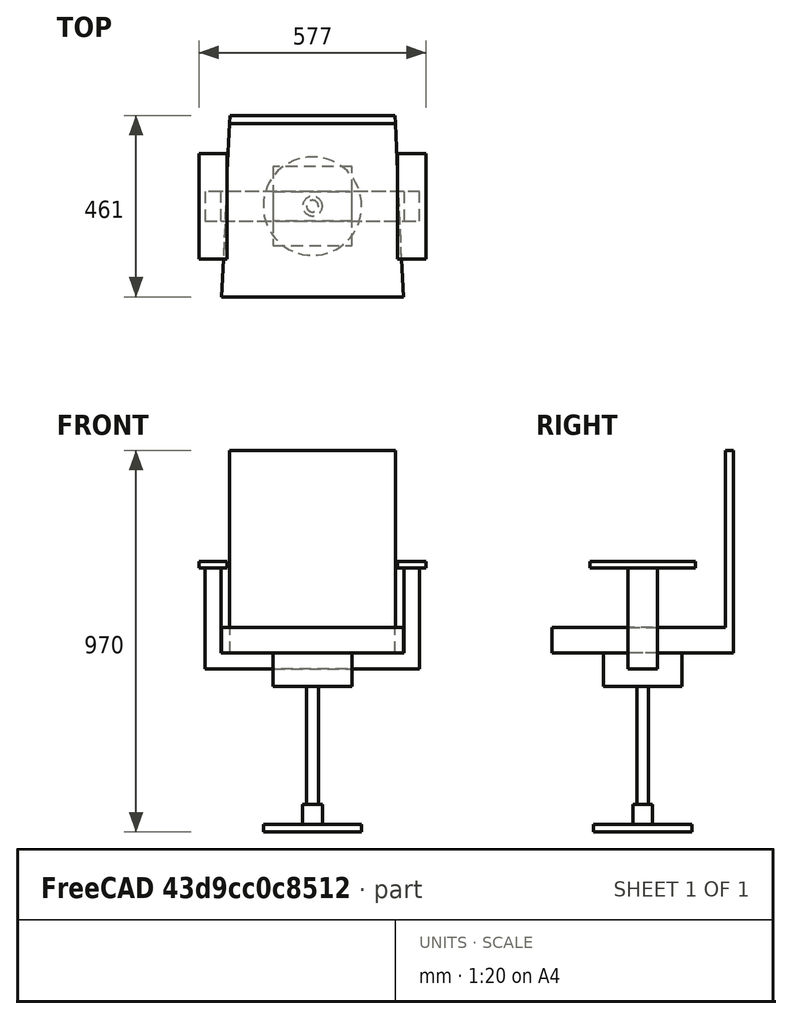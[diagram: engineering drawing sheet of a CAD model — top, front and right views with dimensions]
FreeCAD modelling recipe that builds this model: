
FCSTD DOCUMENT  (FreeCAD 1.0R39109 (Git))
Label: chair02_00503
License: All rights reserved
LicenseURL: https://en.wikipedia.org/wiki/All_rights_reserved
objects: Sketcher::SketchObject×10, PartDesign::Pad×10, TechDraw::DrawViewDimension×9, TechDraw::DrawViewAnnotation×9, PartDesign::Body×5, PartDesign::ShapeBinder×4, TechDraw::DrawSVGTemplate×3, TechDraw::DrawProjGroupItem×3, TechDraw::DrawPage×3, TechDraw::DrawViewSection×3, App::Part×1
note: 77 computed .brp shape members not serialized (recipe doc carries the construction recipe); baked Part::Feature solids carry a one-line shape summary decoded from their .brp

FEATURE [Sketcher::SketchObject] Sketch
  ArcFitTolerance = 1e-06
  AttachmentSupport = -> [XY_Plane]
  FullyConstrained = true
  MakeInternals = false
  MapMode = 5
  sketch-geometry (1):
    g0: Circle CenterX=0 CenterY=0 CenterZ=0 NormalX=0 NormalY=0 NormalZ=1 AngleXU=0 Radius=125
  constraints (2):
    c: Diameter(g0) = 250
    c: Coincident(g0,g-1)
FEATURE [PartDesign::Pad] Pad
  Direction = (0,0,1)
  Length = 20
  Length2 = 10
  Profile = -> Sketch
  ReferenceAxis = -> Sketch [N_Axis]
  Refine = true
  Suppressed = false
  Type = 0
FEATURE [Sketcher::SketchObject] Sketch001
  ArcFitTolerance = 1e-06
  AttachmentSupport = -> [Pad]
  FullyConstrained = true
  MakeInternals = false
  MapMode = 5
  Placement = pos=(0,0,20) rot=(0,0,1;0rad)
  sketch-geometry (1):
    g0: Circle CenterX=0 CenterY=0 CenterZ=0 NormalX=0 NormalY=0 NormalZ=1 AngleXU=0 Radius=25
  constraints (2):
    c: Diameter(g0) = 50
    c: Coincident(g0,g-1)
FEATURE [PartDesign::Pad] Pad001
  BaseFeature = -> Pad
  Direction = (0,0,1)
  Length = 50
  Length2 = 10
  Profile = -> Sketch001
  ReferenceAxis = -> Sketch001 [N_Axis]
  Refine = true
  Suppressed = false
  Type = 0
FEATURE [PartDesign::Body] Body  label="Body1"
  AllowCompound = false
  Group = -> [Sketch,Pad,Sketch001,Pad001]
  Origin = -> Origin
  Tip = -> Pad001
FEATURE [PartDesign::ShapeBinder] CopyPad001  label="Body2_Sketch_P.lane"
  Placement = pos=(0,0,50) rot=(0,0,1;0rad)
  TraceSupport = false
FEATURE [Sketcher::SketchObject] Sketch002
  ArcFitTolerance = 1e-06
  AttachmentSupport = -> [CopyPad001]
  FullyConstrained = true
  MakeInternals = false
  MapMode = 5
  Placement = pos=(0,0,70) rot=(0,0,1;0rad)
  sketch-geometry (1):
    g0: Circle CenterX=0 CenterY=0 CenterZ=0 NormalX=0 NormalY=0 NormalZ=1 AngleXU=0 Radius=15
  constraints (2):
    c: Diameter(g0) = 30
    c: Coincident(g0,g-1)
FEATURE [PartDesign::Pad] Pad002
  Direction = (0,0,1)
  Length = 300
  Length2 = 10
  Placement = pos=(0,0,50) rot=(0,0,1;0rad)
  Profile = -> Sketch002
  ReferenceAxis = -> Sketch002 [N_Axis]
  Refine = true
  Suppressed = false
  Type = 0
FEATURE [PartDesign::Body] Body001  label="Body2"
  AllowCompound = false
  Group = -> [CopyPad001,Sketch002,Pad002]
  Origin = -> Origin001
  Tip = -> Pad002
FEATURE [PartDesign::ShapeBinder] CopyPad002  label="Body3_Sketch_Plane"
  Placement = pos=(0,0,300) rot=(0,0,1;0rad)
  TraceSupport = false
FEATURE [Sketcher::SketchObject] Sketch003
  ArcFitTolerance = 1e-06
  AttachmentSupport = -> [CopyPad002]
  FullyConstrained = true
  MakeInternals = false
  MapMode = 5
  Placement = pos=(0,0,370) rot=(0,0,1;0rad)
  sketch-geometry (5):
    g0: LineSegment StartX=-100 StartY=-100 StartZ=0 EndX=100 EndY=-100 EndZ=0
    g1: LineSegment StartX=100 StartY=-100 StartZ=0 EndX=100 EndY=100 EndZ=0
    g2: LineSegment StartX=100 StartY=100 StartZ=0 EndX=-100 EndY=100 EndZ=0
    g3: LineSegment StartX=-100 StartY=100 StartZ=0 EndX=-100 EndY=-100 EndZ=0
    g4: GeomPoint [constr] X=0 Y=0 Z=0
  constraints (12):
    c: Coincident(g0,g1)
    c: Coincident(g1,g2)
    c: Coincident(g2,g3)
    c: Coincident(g3,g0)
    c: Horizontal(g0)
    c: Horizontal(g2)
    c: Vertical(g1)
    c: Vertical(g3)
    c: Symmetric(g2,g0,g4)
    c: Distance(g1,g3) = 200
    c: Distance(g0,g2) = 200
    c: Coincident(g4,g-1)
FEATURE [PartDesign::Pad] Pad003
  Direction = (0,0,1)
  Length = 45
  Length2 = 10
  Placement = pos=(0,0,300) rot=(0,0,1;0rad)
  Profile = -> Sketch003
  ReferenceAxis = -> Sketch003 [N_Axis]
  Refine = true
  Suppressed = false
  Type = 0
FEATURE [PartDesign::ShapeBinder] CopyPad003  label="Body4_Sketch_Plane"
  Placement = pos=(0,0,45) rot=(0,0,1;0rad)
  TraceSupport = false
FEATURE [Sketcher::SketchObject] Sketch004
  ArcFitTolerance = 1e-06
  AttachmentSupport = -> [CopyPad003]
  FullyConstrained = true
  MakeInternals = false
  MapMode = 5
  Placement = pos=(0,0,415) rot=(0,0,1;0rad)
  sketch-geometry (5):
    g0: LineSegment StartX=-272.5 StartY=-37.5 StartZ=0 EndX=272.5 EndY=-37.5 EndZ=0
    g1: LineSegment StartX=272.5 StartY=-37.5 StartZ=0 EndX=272.5 EndY=37.5 EndZ=0
    g2: LineSegment StartX=272.5 StartY=37.5 StartZ=0 EndX=-272.5 EndY=37.5 EndZ=0
    g3: LineSegment StartX=-272.5 StartY=37.5 StartZ=0 EndX=-272.5 EndY=-37.5 EndZ=0
    g4: GeomPoint [constr] X=0 Y=0 Z=0
  constraints (12):
    c: Coincident(g0,g1)
    c: Coincident(g1,g2)
    c: Coincident(g2,g3)
    c: Coincident(g3,g0)
    c: Horizontal(g0)
    c: Horizontal(g2)
    c: Vertical(g1)
    c: Vertical(g3)
    c: Symmetric(g2,g0,g4)
    c: Distance(g1,g3) = 545
    c: Distance(g0,g2) = 75
    c: Coincident(g4,g-1)
FEATURE [PartDesign::Pad] Pad004
  Direction = (0,0,1)
  Length = 40
  Length2 = 10
  Placement = pos=(0,0,45) rot=(0,0,1;0rad)
  Profile = -> Sketch004
  ReferenceAxis = -> Sketch004 [N_Axis]
  Refine = true
  Suppressed = false
  Type = 0
FEATURE [Sketcher::SketchObject] Sketch005
  ArcFitTolerance = 1e-06
  AttachmentSupport = -> [Pad004]
  ExternalGeometry = -> [Pad004]
  FullyConstrained = true
  MakeInternals = false
  MapMode = 5
  Placement = pos=(0,0,455) rot=(0,0,1;0rad)
  sketch-geometry (8):
    g0: LineSegment StartX=-272.5 StartY=37.5 StartZ=0 EndX=-272.5 EndY=-37.5 EndZ=0
    g1: LineSegment StartX=-272.5 StartY=-37.5 StartZ=0 EndX=-232.5 EndY=-37.5 EndZ=0
    g2: LineSegment StartX=-232.5 StartY=-37.5 StartZ=0 EndX=-232.5 EndY=37.5 EndZ=0
    g3: LineSegment StartX=-232.5 StartY=37.5 StartZ=0 EndX=-272.5 EndY=37.5 EndZ=0
    g4: LineSegment StartX=272.5 StartY=37.5 StartZ=0 EndX=232.5 EndY=37.5 EndZ=0
    g5: LineSegment StartX=232.5 StartY=37.5 StartZ=0 EndX=232.5 EndY=-37.5 EndZ=0
    g6: LineSegment StartX=232.5 StartY=-37.5 StartZ=0 EndX=272.5 EndY=-37.5 EndZ=0
    g7: LineSegment StartX=272.5 StartY=-37.5 StartZ=0 EndX=272.5 EndY=37.5 EndZ=0
  constraints (22):
    c: Coincident(g0,g1)
    c: Coincident(g1,g2)
    c: Coincident(g2,g3)
    c: Coincident(g3,g0)
    c: Vertical(g0)
    c: Vertical(g2)
    c: Horizontal(g1)
    c: Horizontal(g3)
    c: Coincident(g0,g-3)
    c: PointOnObject(g1,g-4)
    c: DistanceX(g3,g3) = 40
    c: Coincident(g4,g5)
    c: Coincident(g5,g6)
    c: Coincident(g6,g7)
    c: Coincident(g7,g4)
    c: Horizontal(g4)
    c: Horizontal(g6)
    c: Vertical(g5)
    c: Vertical(g7)
    c: Coincident(g4,g-3)
    c: PointOnObject(g5,g-4)
    c: Equal(g4,g3)
FEATURE [PartDesign::Pad] Pad005
  BaseFeature = -> Pad004
  Direction = (0,0,1)
  Length = 216
  Length2 = 10
  Placement = pos=(0,0,45) rot=(0,0,1;0rad)
  Profile = -> Sketch005
  ReferenceAxis = -> Sketch005 [N_Axis]
  Refine = true
  Suppressed = false
  Type = 0
FEATURE [Sketcher::SketchObject] Sketch006
  ArcFitTolerance = 1e-06
  AttachmentSupport = -> [Pad005]
  ExternalGeometry = -> [Pad005]
  FullyConstrained = true
  MakeInternals = false
  MapMode = 5
  Placement = pos=(0,0,671) rot=(0,0,1;0rad)
  sketch-geometry (16):
    g0: LineSegment StartX=-288.5 StartY=134 StartZ=0 EndX=-288.5 EndY=-134 EndZ=0
    g1: LineSegment StartX=-288.5 StartY=-134 StartZ=0 EndX=-216.5 EndY=-134 EndZ=0
    g2: LineSegment StartX=-216.5 StartY=-134 StartZ=0 EndX=-216.5 EndY=134 EndZ=0
    g3: LineSegment StartX=-216.5 StartY=134 StartZ=0 EndX=-288.5 EndY=134 EndZ=0
    g4: LineSegment StartX=216.5 StartY=134 StartZ=0 EndX=216.5 EndY=-134 EndZ=0
    g5: LineSegment StartX=216.5 StartY=-134 StartZ=0 EndX=288.5 EndY=-134 EndZ=0
    g6: LineSegment StartX=288.5 StartY=-134 StartZ=0 EndX=288.5 EndY=134 EndZ=0
    g7: LineSegment StartX=288.5 StartY=134 StartZ=0 EndX=216.5 EndY=134 EndZ=0
    g8: LineSegment [constr] StartX=-272.5 StartY=37.5 StartZ=0 EndX=-232.5 EndY=-37.5 EndZ=0
    g9: LineSegment [constr] StartX=-252.5 StartY=0 StartZ=0 EndX=-272.5 EndY=-37.5 EndZ=0
    g10: LineSegment [constr] StartX=232.5 StartY=37.5 StartZ=0 EndX=272.5 EndY=-37.5 EndZ=0
    g11: LineSegment [constr] StartX=272.5 StartY=37.5 StartZ=0 EndX=252.5 EndY=0 EndZ=0
    g12: LineSegment [constr] StartX=-216.5 StartY=134 StartZ=0 EndX=-288.5 EndY=-134 EndZ=0
    g13: LineSegment [constr] StartX=-288.5 StartY=134 StartZ=0 EndX=-252.5 EndY=0 EndZ=0
    g14: LineSegment [constr] StartX=216.5 StartY=134 StartZ=0 EndX=288.5 EndY=-134 EndZ=0
    g15: LineSegment [constr] StartX=288.5 StartY=134 StartZ=0 EndX=252.5 EndY=0 EndZ=0
  constraints (38):
    c: Coincident(g0,g1)
    c: Coincident(g1,g2)
    c: Coincident(g2,g3)
    c: Coincident(g3,g0)
    c: Vertical(g0)
    c: Vertical(g2)
    c: Horizontal(g1)
    c: Horizontal(g3)
    c: Coincident(g4,g5)
    c: Coincident(g5,g6)
    c: Coincident(g6,g7)
    c: Coincident(g7,g4)
    c: Vertical(g4)
    c: Vertical(g6)
    c: Horizontal(g5)
    c: Horizontal(g7)
    c: Equal(g7,g3)
    c: Equal(g2,g4)
    c: DistanceX(g3,g3) = 72
    c: Coincident(g8,g-4)
    c: Coincident(g8,g-3)
    c: Coincident(g9,g-4)
    c: Coincident(g10,g-5)
    c: Coincident(g10,g-6)
    c: Coincident(g11,g-6)
    c: Symmetric(g10,g10,g11)
    c: Symmetric(g8,g8,g9)
    c: Coincident(g12,g2)
    c: Coincident(g12,g0)
    c: Coincident(g13,g0)
    c: Symmetric(g12,g12,g13)
    c: Coincident(g9,g13)
    c: Coincident(g14,g4)
    c: Coincident(g14,g5)
    c: Coincident(g15,g6)
    c: Symmetric(g14,g14,g15)
    c: Coincident(g15,g11)
    c: DistanceY(g2,g2) = 268
FEATURE [PartDesign::Pad] Pad006
  BaseFeature = -> Pad005
  Direction = (0,0,1)
  Length = 17
  Length2 = 10
  Placement = pos=(0,0,45) rot=(0,0,1;0rad)
  Profile = -> Sketch006
  ReferenceAxis = -> Sketch006 [N_Axis]
  Refine = true
  Suppressed = false
  Type = 0
FEATURE [PartDesign::Body] Body003  label="Body4"
  AllowCompound = false
  Group = -> [CopyPad003,Sketch004,Pad004,Sketch005,Pad005,Sketch006,Pad006]
  Origin = -> Origin003
  Tip = -> Pad006
FEATURE [PartDesign::ShapeBinder] CopyPad006  label="Body5_Sketch_Plane"
  Placement = pos=(0,0,45) rot=(0,0,1;0rad)
  TraceSupport = false
FEATURE [Sketcher::SketchObject] Sketch009
  ArcFitTolerance = 1e-06
  AttachmentSupport = -> [Pad003]
  ExternalGeometry = -> [Pad003]
  FullyConstrained = true
  MakeInternals = false
  MapMode = 5
  Placement = pos=(0,0,415) rot=(0,0,1;0rad)
  sketch-geometry (8):
    g0: LineSegment StartX=-100 StartY=100 StartZ=0 EndX=-100 EndY=37.5 EndZ=0
    g1: LineSegment StartX=-100 StartY=37.5 StartZ=0 EndX=100 EndY=37.5 EndZ=0
    g2: LineSegment StartX=100 StartY=37.5 StartZ=0 EndX=100 EndY=100 EndZ=0
    g3: LineSegment StartX=100 StartY=100 StartZ=0 EndX=-100 EndY=100 EndZ=0
    g4: LineSegment StartX=100 StartY=-100 StartZ=0 EndX=100 EndY=-37.5 EndZ=0
    g5: LineSegment StartX=100 StartY=-37.5 StartZ=0 EndX=-100 EndY=-37.5 EndZ=0
    g6: LineSegment StartX=-100 StartY=-37.5 StartZ=0 EndX=-100 EndY=-100 EndZ=0
    g7: LineSegment StartX=-100 StartY=-100 StartZ=0 EndX=100 EndY=-100 EndZ=0
  constraints (21):
    c: Coincident(g0,g1)
    c: Coincident(g1,g2)
    c: Coincident(g2,g3)
    c: Coincident(g3,g0)
    c: Vertical(g0)
    c: Vertical(g2)
    c: Horizontal(g1)
    c: Horizontal(g3)
    c: Coincident(g0,g-3)
    c: PointOnObject(g1,g-4)
    c: Coincident(g4,g5)
    c: Coincident(g5,g6)
    c: Coincident(g6,g7)
    c: Coincident(g7,g4)
    c: Vertical(g6)
    c: Horizontal(g5)
    c: Horizontal(g7)
    c: Coincident(g4,g-4)
    c: PointOnObject(g5,g-3)
    c: DistanceY(g4,g1) = 75
    c: Symmetric(g1,g4,g-1)
FEATURE [PartDesign::Pad] Pad009
  BaseFeature = -> Pad003
  Direction = (0,0,1)
  Length = 40
  Length2 = 10
  Placement = pos=(0,0,300) rot=(0,0,1;0rad)
  Profile = -> Sketch009
  ReferenceAxis = -> Sketch009 [N_Axis]
  Refine = true
  Suppressed = false
  Type = 0
FEATURE [PartDesign::Body] Body002  label="Body3"
  AllowCompound = false
  Group = -> [CopyPad002,Sketch003,Pad003,Sketch009,Pad009]
  Origin = -> Origin002
  Tip = -> Pad009
FEATURE [Sketcher::SketchObject] Sketch007
  ArcFitTolerance = 1e-06
  AttachmentSupport = -> [CopyPad006]
  FullyConstrained = true
  MakeInternals = false
  MapMode = 5
  Placement = pos=(0,0,455) rot=(0,0,1;0rad)
  sketch-geometry (8):
    g0: LineSegment StartX=-210 StartY=230.5 StartZ=0 EndX=-231 EndY=-230.5 EndZ=0
    g1: LineSegment StartX=-231 StartY=-230.5 StartZ=0 EndX=231 EndY=-230.5 EndZ=0
    g2: LineSegment StartX=231 StartY=-230.5 StartZ=0 EndX=210 EndY=230.5 EndZ=0
    g3: LineSegment StartX=210 StartY=230.5 StartZ=0 EndX=-210 EndY=230.5 EndZ=0
    g4: LineSegment [constr] StartX=210 StartY=230.5 StartZ=0 EndX=2.84e-14 EndY=0 EndZ=0
    g5: LineSegment [constr] StartX=2.84e-14 StartY=0 StartZ=0 EndX=-210 EndY=230.5 EndZ=0
    g6: LineSegment [constr] StartX=210 StartY=230.5 StartZ=0 EndX=210 EndY=0 EndZ=0
    g7: LineSegment [constr] StartX=231 StartY=-230.5 StartZ=0 EndX=231 EndY=0 EndZ=0
  constraints (20):
    c: Coincident(g2,g1)
    c: DistanceX(g1,g1) = 462
    c: DistanceX(g3,g3) = 420
    c: Coincident(g1,g0)
    c: Symmetric(g2,g0,g-2)
    c: Coincident(g2,g3)
    c: Coincident(g3,g0)
    c: Coincident(g4,g2)
    c: Coincident(g4,g-1)
    c: Coincident(g5,g4)
    c: Coincident(g5,g0)
    c: DistanceY(g2,g2) = 461
    c: Coincident(g6,g2)
    c: PointOnObject(g6,g-1)
    c: Vertical(g6)
    c: Coincident(g7,g1)
    c: PointOnObject(g7,g-1)
    c: Vertical(g7)
    c: Equal(g7,g6)
    c: Symmetric(g1,g0,g-2)
FEATURE [PartDesign::Pad] Pad007
  Direction = (0,0,1)
  Length = 65
  Length2 = 10
  Placement = pos=(0,0,45) rot=(0,0,1;0rad)
  Profile = -> Sketch007
  ReferenceAxis = -> Sketch007 [N_Axis]
  Refine = true
  Suppressed = false
  Type = 0
FEATURE [Sketcher::SketchObject] Sketch008
  ArcFitTolerance = 1e-06
  AttachmentSupport = -> [Pad007]
  ExternalGeometry = -> [Pad007]
  FullyConstrained = true
  MakeInternals = false
  MapMode = 5
  Placement = pos=(0,0,520) rot=(0,0,1;0rad)
  sketch-geometry (4):
    g0: LineSegment StartX=-210 StartY=230.5 StartZ=0 EndX=210 EndY=230.5 EndZ=0
    g1: LineSegment StartX=-210 StartY=230.5 StartZ=0 EndX=-210.957 EndY=209.5 EndZ=0
    g2: LineSegment StartX=-210.957 StartY=209.5 StartZ=0 EndX=210.957 EndY=209.5 EndZ=0
    g3: LineSegment StartX=210 StartY=230.5 StartZ=0 EndX=210.957 EndY=209.5 EndZ=0
  constraints (10):
    c: Coincident(g0,g-3)
    c: Coincident(g0,g-4)
    c: Coincident(g1,g0)
    c: PointOnObject(g1,g-3)
    c: Coincident(g2,g1)
    c: PointOnObject(g2,g-4)
    c: Horizontal(g2)
    c: Coincident(g3,g0)
    c: Coincident(g3,g2)
    c: DistanceY(g1,g1) = 21
FEATURE [PartDesign::Pad] Pad008
  BaseFeature = -> Pad007
  Direction = (0,0,1)
  Length = 450
  Length2 = 10
  Placement = pos=(0,0,45) rot=(0,0,1;0rad)
  Profile = -> Sketch008
  ReferenceAxis = -> Sketch008 [N_Axis]
  Refine = true
  Suppressed = false
  Type = 0
FEATURE [PartDesign::Body] Body004  label="Body5"
  AllowCompound = false
  Group = -> [CopyPad006,Sketch007,Pad007,Sketch008,Pad008]
  Origin = -> Origin004
  Tip = -> Pad008
FEATURE [App::Part] Part  label="chair02"
  Group = -> [Body,Body001,Body002,Body003,Body004]
  Origin = -> Origin005
FEATURE [TechDraw::DrawSVGTemplate] Template  label="テンプレート"
  Height = 210
  Orientation = 1
  Template = <userpath>/AppData/Local/Programs/FreeCAD 1.0/data/Mod/TechDraw/Templates/A4_Landscape_blank.svg
  Width = 297
FEATURE [TechDraw::DrawProjGroupItem] View
  CoarseView = false
  Direction = (0,0,1)
  Focus = 100
  HardHidden = true
  IsoCount = 0
  IsoHidden = false
  IsoVisible = false
  LockPosition = false
  Perspective = false
  Rotation = 0
  RotationVector = (1,0,0)
  Scale = 0.333333
  ScaleType = 2
  ScrubCount = 1
  SeamHidden = false
  SeamVisible = false
  SmoothHidden = false
  SmoothVisible = true
  Source = -> [Part]
  Type = 0
  X = 131.425
  XDirection = (1,0,0)
  Y = 107.897
FEATURE [TechDraw::DrawViewDimension] Dimension004  label="寸法004"
  AngleOverride = false
  Arbitrary = false
  ArbitraryTolerances = false
  BoxCorners = (2) [(-96.1666,-76.8333,0),(96.1666,76.8333,0)]
  EqualTolerance = true
  ExtensionAngle = 0
  FormatSpec = %.2w
  FormatSpecOverTolerance = %+.2w
  FormatSpecUnderTolerance = %+.2w
  Inverted = false
  LineAngle = 0
  LockPosition = false
  MeasureType = 1
  OverTolerance = 0
  References2D = -> [View]
  Rotation = 0
  Scale = 0.2
  ScaleType = 2
  TheoreticalExact = false
  Type = 1
  UnderTolerance = 0
  X = -84.1666
  Y = 58.5053
FEATURE [TechDraw::DrawViewDimension] Dimension005  label="寸法005"
  AngleOverride = false
  Arbitrary = false
  ArbitraryTolerances = false
  BoxCorners = (2) [(-96.1666,-76.8333,0),(96.1666,76.8333,0)]
  EqualTolerance = true
  ExtensionAngle = 0
  FormatSpec = %.2w
  FormatSpecOverTolerance = %+.2w
  FormatSpecUnderTolerance = %+.2w
  Inverted = false
  LineAngle = 0
  LockPosition = false
  MeasureType = 1
  OverTolerance = 0
  References2D = -> [View]
  Rotation = 0
  Scale = 0.2
  ScaleType = 2
  TheoreticalExact = false
  Type = 2
  UnderTolerance = 0
  X = -108.801
  Y = 0
FEATURE [TechDraw::DrawPage] Page  label="用紙"
  KeepUpdated = true
  NextBalloonIndex = 1
  ProjectionType = 0
  Template = -> Template
  Views = -> [View,Dimension004,Dimension005]
FEATURE [TechDraw::DrawSVGTemplate] Template001  label="テンプレート001"
  Height = 210
  Orientation = 1
  Template = <userpath>/AppData/Local/Programs/FreeCAD 1.0/data/Mod/TechDraw/Templates/A4_Landscape_blank.svg
  Width = 297
FEATURE [TechDraw::DrawSVGTemplate] Template002  label="テンプレート002"
  Height = 210
  Orientation = 1
  Template = <userpath>/AppData/Local/Programs/FreeCAD 1.0/data/Mod/TechDraw/Templates/A4_Landscape_blank.svg
  Width = 297
FEATURE [TechDraw::DrawProjGroupItem] View001
  CoarseView = false
  Direction = (0,-1,0)
  Focus = 100
  HardHidden = true
  IsoCount = 0
  IsoHidden = false
  IsoVisible = false
  LockPosition = false
  Perspective = false
  Rotation = 0
  RotationVector = (1,0,0)
  Scale = 0.2
  ScaleType = 2
  ScrubCount = 1
  SeamHidden = false
  SeamVisible = false
  SmoothHidden = false
  SmoothVisible = true
  Source = -> [Part]
  Type = 0
  X = 72.2264
  XDirection = (1,0,0)
  Y = 108.632
FEATURE [TechDraw::DrawViewSection] SectionView  label="セクション  - "
  BaseView = -> View001
  CoarseView = false
  CutSurfaceDisplay = 2
  Direction = (1e-16,0,1)
  FileGeomPattern = <userpath>\AppData\Local\Programs\FreeCAD 1.0\data\Mod/TechDraw/PAT/FCPAT.pat
  FileHatchPattern = <userpath>\AppData\Local\Programs\FreeCAD 1.0\data\Mod/TechDraw/Patterns/simple.svg
  Focus = 100
  FuseBeforeCut = false
  HardHidden = true
  HatchOffset = (0,0,0)
  HatchRotation = 0
  HatchScale = 1
  IsoCount = 0
  IsoHidden = false
  IsoVisible = false
  LockPosition = false
  NameGeomPattern = Diamond
  Perspective = false
  Rotation = 0
  Scale = 0.15
  ScaleType = 2
  ScrubCount = 1
  SeamHidden = false
  SeamVisible = false
  SectionDirection = 4
  SectionLineStretch = 1
  SectionNormal = (1e-16,0,1)
  SectionOrigin = (0,0,581)
  SmoothHidden = false
  SmoothVisible = true
  Source = -> [Part]
  TrimAfterCut = false
  UsePreviousCut = false
  X = 215.858
  XDirection = (1,0,-1e-16)
  Y = 166.085
FEATURE [TechDraw::DrawViewSection] SectionView001  label="セクション001  - "
  BaseView = -> View001
  CoarseView = false
  CutSurfaceDisplay = 2
  Direction = (1e-16,0,1)
  FileGeomPattern = <userpath>\AppData\Local\Programs\FreeCAD 1.0\data\Mod/TechDraw/PAT/FCPAT.pat
  FileHatchPattern = <userpath>\AppData\Local\Programs\FreeCAD 1.0\data\Mod/TechDraw/Patterns/simple.svg
  Focus = 100
  FuseBeforeCut = false
  HardHidden = true
  HatchOffset = (0,0,0)
  HatchRotation = 0
  HatchScale = 1
  IsoCount = 0
  IsoHidden = false
  IsoVisible = false
  LockPosition = false
  NameGeomPattern = Diamond
  Perspective = false
  Rotation = 0
  Scale = 0.15
  ScaleType = 2
  ScrubCount = 1
  SeamHidden = false
  SeamVisible = false
  SectionDirection = 4
  SectionLineStretch = 1
  SectionNormal = (1e-16,0,1)
  SectionOrigin = (0,0,437)
  SmoothHidden = false
  SmoothVisible = true
  Source = -> [Part]
  TrimAfterCut = false
  UsePreviousCut = false
  X = 215.086
  XDirection = (1,0,-1e-16)
  Y = 92.3168
FEATURE [TechDraw::DrawViewSection] SectionView002  label="セクション002  - "
  BaseView = -> View001
  CoarseView = false
  CutSurfaceDisplay = 2
  Direction = (1e-16,0,1)
  FileGeomPattern = <userpath>\AppData\Local\Programs\FreeCAD 1.0\data\Mod/TechDraw/PAT/FCPAT.pat
  FileHatchPattern = <userpath>\AppData\Local\Programs\FreeCAD 1.0\data\Mod/TechDraw/Patterns/simple.svg
  Focus = 100
  FuseBeforeCut = false
  HardHidden = true
  HatchOffset = (0,0,0)
  HatchRotation = 0
  HatchScale = 1
  IsoCount = 0
  IsoHidden = false
  IsoVisible = false
  LockPosition = false
  NameGeomPattern = Diamond
  Perspective = false
  Rotation = 0
  Scale = 0.15
  ScaleType = 2
  ScrubCount = 1
  SeamHidden = false
  SeamVisible = false
  SectionDirection = 4
  SectionLineStretch = 1
  SectionNormal = (1e-16,0,1)
  SectionOrigin = (0,0,200)
  SmoothHidden = false
  SmoothVisible = true
  Source = -> [Part]
  TrimAfterCut = false
  UsePreviousCut = false
  X = 214.868
  XDirection = (1,0,-1e-16)
  Y = 24.434
FEATURE [TechDraw::DrawViewDimension] Dimension007  label="寸法007"
  AngleOverride = false
  Arbitrary = false
  ArbitraryTolerances = false
  BoxCorners = (2) [(-40.875,-34.575,0),(40.875,34.575,0)]
  EqualTolerance = true
  ExtensionAngle = 0
  FormatSpec = %.2w
  FormatSpecOverTolerance = %+.2w
  FormatSpecUnderTolerance = %+.2w
  Inverted = false
  LineAngle = 0
  LockPosition = false
  MeasureType = 1
  OverTolerance = 0
  References2D = -> [SectionView]
  Rotation = 0
  Scale = 0.2
  ScaleType = 2
  TheoreticalExact = false
  Type = 1
  UnderTolerance = 0
  X = 48.3858
  Y = 24.3952
FEATURE [TechDraw::DrawViewDimension] Dimension008  label="寸法008"
  AngleOverride = false
  Arbitrary = false
  ArbitraryTolerances = false
  BoxCorners = (2) [(-40.875,-34.575,0),(40.875,34.575,0)]
  EqualTolerance = true
  ExtensionAngle = 0
  FormatSpec = %.2w
  FormatSpecOverTolerance = %+.2w
  FormatSpecUnderTolerance = %+.2w
  Inverted = false
  LineAngle = 0
  LockPosition = false
  MeasureType = 1
  OverTolerance = 0
  References2D = -> [SectionView]
  Rotation = 0
  Scale = 0.2
  ScaleType = 2
  TheoreticalExact = false
  Type = 2
  UnderTolerance = 0
  X = 59.3049
  Y = -11.5187
FEATURE [TechDraw::DrawViewDimension] Dimension009  label="寸法009"
  AngleOverride = false
  Arbitrary = false
  ArbitraryTolerances = false
  BoxCorners = (2) [(-40.875,-18.75,0),(40.875,18.75,0)]
  EqualTolerance = true
  ExtensionAngle = 0
  FormatSpec = %.2w
  FormatSpecOverTolerance = %+.2w
  FormatSpecUnderTolerance = %+.2w
  Inverted = false
  LineAngle = 0
  LockPosition = false
  MeasureType = 1
  OverTolerance = 0
  References2D = -> [SectionView001]
  Rotation = 0
  Scale = 0.2
  ScaleType = 2
  TheoreticalExact = false
  Type = 1
  UnderTolerance = 0
  X = 0
  Y = -24.3529
FEATURE [TechDraw::DrawViewDimension] Dimension011  label="寸法011"
  AngleOverride = false
  Arbitrary = false
  ArbitraryTolerances = false
  BoxCorners = (2) [(-40.875,-18.75,0),(40.875,18.75,0)]
  EqualTolerance = true
  ExtensionAngle = 0
  FormatSpec = %.2w
  FormatSpecOverTolerance = %+.2w
  FormatSpecUnderTolerance = %+.2w
  Inverted = false
  LineAngle = 0
  LockPosition = false
  MeasureType = 1
  OverTolerance = 0
  References2D = -> [SectionView001]
  Rotation = 0
  Scale = 0.2
  ScaleType = 2
  TheoreticalExact = false
  Type = 2
  UnderTolerance = 0
  X = 58.5124
  Y = 0
FEATURE [TechDraw::DrawViewAnnotation] Annotation  label="注釈"
  Font = osifont
  LineSpace = 100
  LockPosition = false
  MaxWidth = -1
  Rotation = 0
  Scale = 0.2
  ScaleType = 2
  Text = A
  TextSize = 5
  TextStyle = 0
  X = 143.937
  Y = 118.99
FEATURE [TechDraw::DrawViewAnnotation] Annotation001  label="注釈001"
  Font = osifont
  LineSpace = 100
  LockPosition = false
  MaxWidth = -1
  Rotation = 0
  Scale = 0.2
  ScaleType = 2
  Text = A
  TextSize = 5
  TextStyle = 0
  X = 9.25009
  Y = 118.99
FEATURE [TechDraw::DrawViewAnnotation] Annotation002  label="注釈002"
  Font = osifont
  LineSpace = 100
  LockPosition = false
  MaxWidth = -1
  Rotation = 0
  Scale = 0.2
  ScaleType = 2
  Text = B
  TextSize = 5
  TextStyle = 0
  X = 9.25009
  Y = 89.4351
FEATURE [TechDraw::DrawViewAnnotation] Annotation003  label="注釈003"
  Font = osifont
  LineSpace = 100
  LockPosition = false
  MaxWidth = -1
  Rotation = 0
  Scale = 0.2
  ScaleType = 2
  Text = B
  TextSize = 5
  TextStyle = 0
  X = 145.458
  Y = 89.4351
FEATURE [TechDraw::DrawViewAnnotation] Annotation004  label="注釈004"
  Font = osifont
  LineSpace = 100
  LockPosition = false
  MaxWidth = -1
  Rotation = 0
  Scale = 0.2
  ScaleType = 2
  Text = C
  TextSize = 5
  TextStyle = 0
  X = 145.458
  Y = 40.7495
FEATURE [TechDraw::DrawViewAnnotation] Annotation005  label="注釈005"
  Font = osifont
  LineSpace = 100
  LockPosition = false
  MaxWidth = -1
  Rotation = 0
  Scale = 0.2
  ScaleType = 2
  Text = C
  TextSize = 5
  TextStyle = 0
  X = 9.25009
  Y = 43.6474
FEATURE [TechDraw::DrawViewAnnotation] Annotation006  label="注釈006"
  Font = osifont
  LineSpace = 100
  LockPosition = false
  MaxWidth = -1
  Rotation = 0
  Scale = 0.2
  ScaleType = 2
  Text = A-A
  TextSize = 5
  TextStyle = 0
  X = 215.858
  Y = 205.891
FEATURE [TechDraw::DrawViewAnnotation] Annotation007  label="注釈007"
  Font = osifont
  LineSpace = 100
  LockPosition = false
  MaxWidth = -1
  Rotation = 0
  Scale = 0.2
  ScaleType = 2
  Text = B-B
  TextSize = 5
  TextStyle = 0
  X = 215.858
  Y = 117.871
FEATURE [TechDraw::DrawViewAnnotation] Annotation008  label="注釈008"
  Font = osifont
  LineSpace = 100
  LockPosition = false
  MaxWidth = -1
  Rotation = 0
  Scale = 0.2
  ScaleType = 2
  Text = C -C
  TextSize = 5
  TextStyle = 0
  X = 215.858
  Y = 48.4539
FEATURE [TechDraw::DrawPage] Page002  label="用紙002"
  KeepUpdated = true
  NextBalloonIndex = 1
  ProjectionType = 0
  Template = -> Template002
  Views = -> [View001,SectionView,SectionView001,SectionView002,Dimension007,Dimension008,Dimension009,Dimension011,Annotation,Annotation001,Annotation002,Annotation003,Annotation004,Annotation005,Annotation006,Annotation007,Annotation008]
FEATURE [TechDraw::DrawProjGroupItem] View002
  CoarseView = false
  Direction = (0,-1,0)
  Focus = 100
  HardHidden = true
  IsoCount = 0
  IsoHidden = false
  IsoVisible = false
  LockPosition = false
  Perspective = false
  Rotation = 0
  RotationVector = (1,0,0)
  Scale = 0.2
  ScaleType = 2
  ScrubCount = 1
  SeamHidden = false
  SeamVisible = false
  SmoothHidden = false
  SmoothVisible = true
  Source = -> [Part]
  Type = 0
  X = 144.274
  XDirection = (1,0,0)
  Y = 104.736
FEATURE [TechDraw::DrawViewDimension] Dimension027  label="寸法027"
  AngleOverride = false
  Arbitrary = false
  ArbitraryTolerances = false
  BoxCorners = (2) [(-48.0834,-80.8335,-1e-07),(48.0834,80.8335,1e-07)]
  EqualTolerance = true
  ExtensionAngle = 0
  FormatSpec = %.2w
  FormatSpecOverTolerance = %+.2w
  FormatSpecUnderTolerance = %+.2w
  Inverted = false
  LineAngle = 0
  LockPosition = false
  MeasureType = 1
  OverTolerance = 0
  References2D = -> [View002]
  Rotation = 0
  Scale = 0.2
  ScaleType = 2
  TheoreticalExact = false
  Type = 2
  UnderTolerance = 0
  X = -107.03
  Y = 11.6
FEATURE [TechDraw::DrawViewDimension] Dimension028  label="寸法028"
  AngleOverride = false
  Arbitrary = false
  ArbitraryTolerances = false
  BoxCorners = (2) [(-48.0834,-80.8335,-1e-07),(48.0834,80.8335,1e-07)]
  EqualTolerance = true
  ExtensionAngle = 0
  FormatSpec = %.2w
  FormatSpecOverTolerance = %+.2w
  FormatSpecUnderTolerance = %+.2w
  Inverted = false
  LineAngle = 0
  LockPosition = false
  MeasureType = 1
  OverTolerance = 0
  References2D = -> [View002]
  Rotation = 0
  Scale = 0.2
  ScaleType = 2
  TheoreticalExact = false
  Type = 2
  UnderTolerance = 0
  X = -78.5928
  Y = 52.695
FEATURE [TechDraw::DrawViewDimension] Dimension029  label="寸法029"
  AngleOverride = false
  Arbitrary = false
  ArbitraryTolerances = false
  BoxCorners = (2) [(-48.0834,-80.8335,-1e-07),(48.0834,80.8335,1e-07)]
  EqualTolerance = true
  ExtensionAngle = 0
  FormatSpec = %.2w
  FormatSpecOverTolerance = %+.2w
  FormatSpecUnderTolerance = %+.2w
  Inverted = false
  LineAngle = 0
  LockPosition = false
  MeasureType = 1
  OverTolerance = 0
  References2D = -> [View002]
  Rotation = 0
  Scale = 0.2
  ScaleType = 2
  TheoreticalExact = false
  Type = 2
  UnderTolerance = 0
  X = -78.5928
  Y = 1.03446
FEATURE [TechDraw::DrawPage] Page001  label="用紙001"
  KeepUpdated = true
  NextBalloonIndex = 1
  ProjectionType = 0
  Template = -> Template001
  Views = -> [View002,Dimension027,Dimension028,Dimension029]
